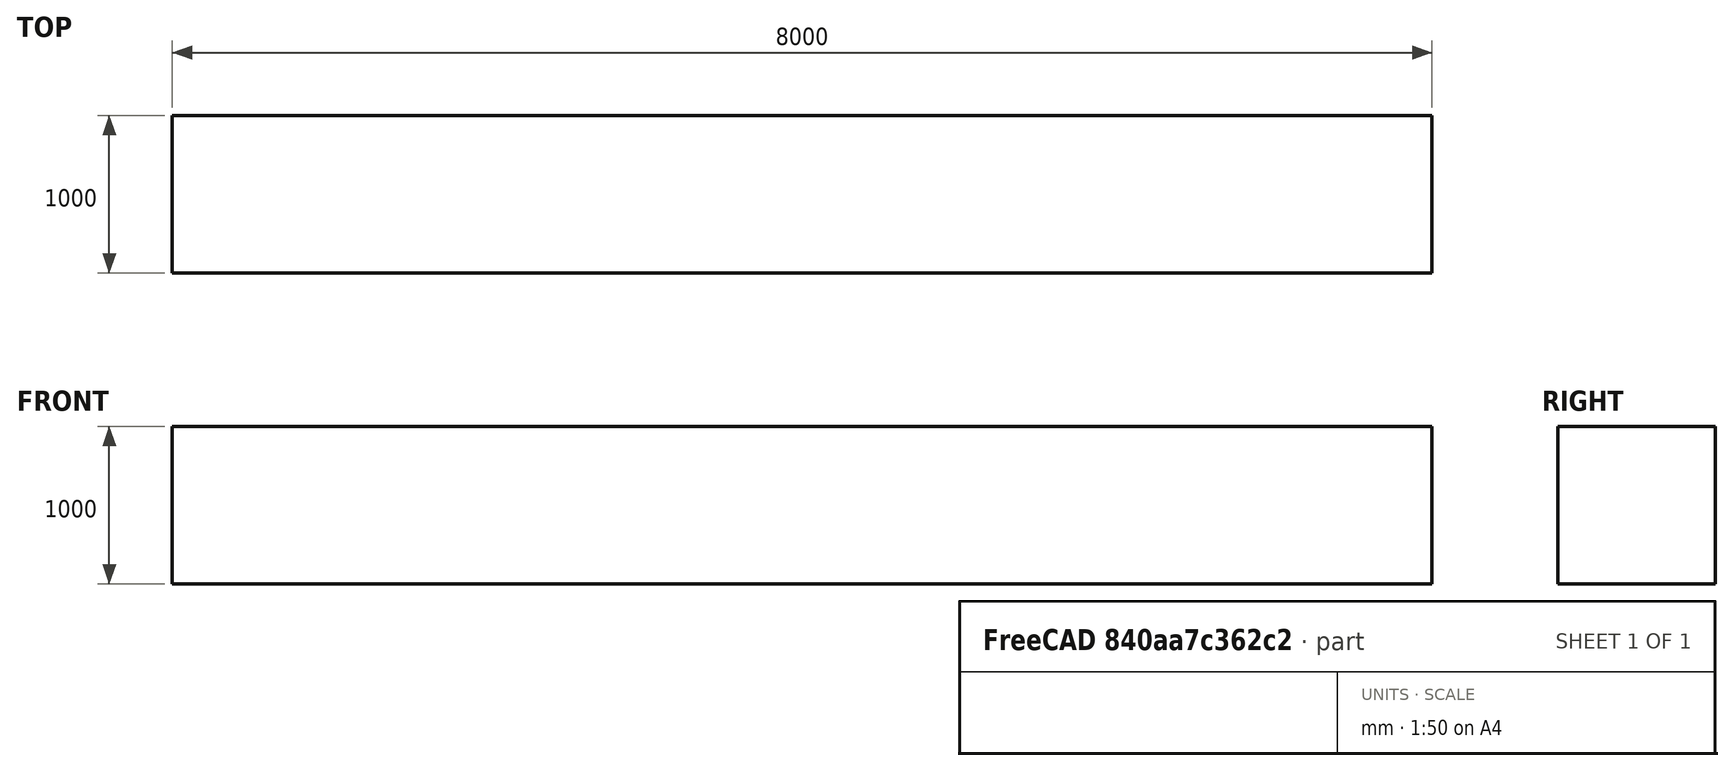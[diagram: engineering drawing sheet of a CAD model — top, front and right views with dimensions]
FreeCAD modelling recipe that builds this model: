
FCSTD DOCUMENT  (FreeCAD 0.19R17171 (Git))
Label: FemCalculixCantilever3D_newSolver
License: CC-BY 3.0
LicenseURL: http://creativecommons.org/licenses/by/3.0/
objects: Fem::FemSolverObjectPython×3, Fem::FemMeshObjectPython×3, Fem::FemResultObjectPython×2, Part::Box×1, Fem::ConstraintFixed×1, Fem::ConstraintForce×1, App::FeaturePython×1, App::MaterialObjectPython×1, Fem::FemPostPipeline×1, Fem::FemAnalysis×1
note: 1 computed .brp shape members not serialized (recipe doc carries the construction recipe); baked Part::Feature solids carry a one-line shape summary decoded from their .brp

FEATURE [Part::Box] Box  label="Cube"
  AttacherType = Attacher::AttachEngine3D
  Height = 1000
  Length = 8000
  Width = 1000
FEATURE [Fem::ConstraintFixed] FemConstraintFixed
  NormalDirection = (-1,0,0)
  Normals = (16) [(-1,0,0),(-1,0,0),(-1,0,0),(-1,0,0),(-1,0,0),(-1,0,0),(-1,0,0),(-1,0,0),(-1,0,0),(-1,0,0),(-1,0,0),(-1,0,0),(-1,0,0),(-1,0,0),(-1,0,0),(-1,0,0)]
  Points = (16) [(0,1000,0),(0,1000,333.333),(0,1000,666.667),(0,1000,1000),(0,666.667,0),(0,666.667,333.333),(0,666.667,666.667),(0,666.667,1000),(0,333.333,0),+7 more]
  References = -> [Box]
  Scale = 33
FEATURE [Fem::ConstraintForce] FemConstraintForce
  Direction = -> Box [Edge7]
  DirectionVector = (0,0,-1)
  Force = 9000000
  NormalDirection = (1,0,0)
  Points = (16) [(8000,1000,0),(8000,1000,333.333),(8000,1000,666.667),(8000,1000,1000),(8000,666.667,0),(8000,666.667,333.333),(8000,666.667,666.667),+9 more]
  References = -> [Box]
  Reversed = true
  Scale = 33
FEATURE [Fem::FemSolverObjectPython] SolverCalculiX  # FEM object (typed FeaturePython)
  AnalysisType = 0
  BeamShellResultOutput3D = false
  EigenmodeHighLimit = 0
  EigenmodeLowLimit = 0
  EigenmodesCount = 15
  GeometricalNonlinearity = 0
  IterationsControlParameterCutb = 0.25,0.5,0.75,0.85,,,1.5,
  IterationsControlParameterIter = 4,8,9,200,10,400,,200,,
  IterationsControlParameterTimeUse = false
  IterationsThermoMechMaximum = 2000
  IterationsUserDefinedIncrementations = false
  IterationsUserDefinedTimeStepLength = false
  MaterialNonlinearity = 0
  MatrixSolverType = 0
  SplitInputWriter = false
  ThermoMechSteadyState = true
  TimeEnd = 1
  TimeInitialStep = 1
FEATURE [Fem::FemSolverObjectPython] SolverZ88  # FEM object (typed FeaturePython)
  AnalysisType = 0
FEATURE [App::FeaturePython] Elasticity  # WARN: FeaturePython — macro-defined, semantics opaque (R4)
  BiCGstablDegree = 0
  Bubbles = false
  CalculatePangle = false
  CalculatePrincipal = false
  CalculateStrains = false
  CalculateStresses = false
  DoFrequencyAnalysis = false
  EigenmodesCount = 5
  LinearDirectMethod = 0
  LinearIterations = 500
  LinearIterativeMethod = 2
  LinearPreconditioning = 2
  LinearSolverType = 1
  LinearTolerance = 1e-08
  Priority = 10
  Stabilize = true
  SteadyStateTolerance = 1e-05
FEATURE [App::MaterialObjectPython] SolidMaterial  # material (typed FeaturePython)
  Category = 0
  Material = Density=7900.0 kg/m^3,Description=Standard steel material for CalculiX sample calculations,Father=Metal,Name=CalculiX-Steel,PoissonRatio=0.3,+4 more (map truncated)
FEATURE [Fem::FemMeshObjectPython] FEMMeshGmsh  # FEM object (typed FeaturePython)
  Algorithm2D = 0
  Algorithm3D = 0
  CharacteristicLengthMax = 0
  CharacteristicLengthMin = 0
  CoherenceMesh = true
  ElementDimension = 0
  ElementOrder = 1
  GeometryTolerance = 1e-06
  GroupsOfNodes = false
  HighOrderOptimize = false
  OptimizeNetgen = false
  OptimizeStd = true
  Part = -> Box
  RecombineAll = false
FEATURE [Fem::FemPostPipeline] SolverElmerResult
  Mode = 0
FEATURE [Fem::FemSolverObjectPython] SolverElmer  # FEM object (typed FeaturePython)
  ElmerResult = -> SolverElmerResult
  Group = -> [Elasticity]
  SteadyStateMaxIterations = 1
  SteadyStateMinIterations = 0
FEATURE [Fem::FemMeshObjectPython] Result_mesh  # FEM object (typed FeaturePython)
FEATURE [Fem::FemResultObjectPython] CalculiX_static_results  # FEM object (typed FeaturePython)
  DisplacementLengths = [0,0,0,0,87.937,87.9368,87.938,87.9383,0,0,0,0,0,0,0,0,0,0,0,0,87.5423,87.6436,87.6436,87.943,87.9418,87.9423,87.5435,87.6449,87.6448,87.9437,87.9421,87.9428,1.98318,5.68761,11.3939,18.906,28.0027,38.4037,49.8592,62.1074,74.8816,0.880806,+478 more]
  DisplacementVectors = (520) [(0,0,0),(0,0,0),(0,0,0),(0,0,0),(8.16317,0.00342817,-87.5573),(-8.1624,-0.00296136,-87.5572),(8.16362,-0.0026403,-87.5583),+513 more]
  Eigenmode = 0
  EigenmodeFrequency = 0
  MaxShear = [175.647,175.645,175.686,175.688,4.51499,4.58967,4.51746,4.67791,41.5712,86.6878,86.7027,145.847,146.892,146.912,41.5961,86.7112,86.7243,145.85,146.913,146.934,14.4288,9.69506,9.67773,6.30296,4.97789,5.00467,14.3519,9.6531,9.64731,6.38343,+490 more]
  Mesh = -> Result_mesh
  NodeNumbers = [1,2,3,4,5,6,7,8,9,10,11,12,13,14,15,16,17,18,19,20,21,22,23,24,25,26,27,28,29,30,31,32,33,34,35,36,37,38,39,40,41,42,43,44,45,46,47,48,49,50,51,52,53,54,55,56,57,58,59,60,61,62,63,64,65,66,67,68,69,+451 more]
  NodeStrainXX = [0.00178534,-0.00178542,0.0017858,-0.00178591,2.55731e-05,-2.6777e-05,2.60379e-05,-2.78694e-05,-6.62106e-08,-0.000893669,0.000893669,0.00158243,0.00162959,0.00162991,-4.29182e-08,-0.000893927,0.000893939,-0.00158248,-0.00162988,-0.00163023,+500 more]
  NodeStrainXY = [0.000338919,-0.000338841,-0.000338881,0.000338842,-6.24106e-06,7.20301e-06,5.95082e-06,-7.54054e-06,3.8554e-08,-0.000204328,0.000204485,1.06174e-07,0.000146602,-0.000146446,-4.03049e-08,0.000204291,-0.000204438,-8.30874e-08,-0.000146496,+501 more]
  NodeStrainXZ = [-6.75804e-05,-6.76787e-05,-6.76474e-05,-6.76703e-05,-1.60131e-05,-1.50392e-05,-1.61571e-05,-1.51969e-05,0.000257345,0.0002158,0.000215887,-0.000434903,-0.000376175,-0.000376179,0.0002575,0.000215933,0.000215976,-0.000434893,-0.000376205,+501 more]
  NodeStrainYY = [-0.000111636,0.000111593,-0.000111609,0.000111601,-3.55842e-06,3.91033e-06,-3.54351e-06,4.16606e-06,2.66083e-14,-6.95479e-10,6.95447e-10,1.51246e-09,1.57275e-09,1.57336e-09,-3.65614e-14,-6.95718e-10,6.95545e-10,-1.51159e-09,-1.57186e-09,+501 more]
  NodeStrainYZ = [-0.00011373,-0.000113706,0.00011372,0.000113715,-1.23872e-06,-4.54037e-07,4.7524e-07,-4.95007e-07,-1.76978e-10,-2.80391e-10,-2.80793e-10,-1.71255e-13,2.54542e-10,-2.54735e-10,1.76364e-10,2.79861e-10,2.80325e-10,-5.89765e-14,2.54579e-10,+501 more]
  NodeStrainZZ = [-0.000259206,0.000259149,-0.000259287,0.000259225,-1.85744e-05,1.95617e-05,-1.82326e-05,1.95673e-05,-4.52237e-13,-4.46011e-10,4.4508e-10,2.98021e-09,3.22873e-09,3.22896e-09,-2.82001e-13,-4.4624e-10,4.45783e-10,-2.98056e-09,-3.22912e-09,+501 more]
  NodeStressXX = [459.773,-459.807,459.898,-459.936,4.54783,-4.72592,4.72246,-5.00309,-0.0187173,-252.634,252.633,447.341,460.673,460.764,-0.0121327,-252.706,252.71,-447.355,-460.756,-460.854,-0.101075,-2.58096,2.3452,3.86865,4.10517,4.15412,0.000454672,+493 more]
  NodeStressXY = [54.7484,-54.7359,-54.7423,54.7361,-1.00817,1.16356,0.961287,-1.21809,0.00622796,-33.0068,33.0321,0.0171512,23.6819,-23.6567,-0.00651079,33.0008,-33.0246,-0.0134218,-23.6648,23.6443,-0.131759,0.240361,-0.375904,0.00314049,-0.486655,0.488129,+494 more]
  NodeStressXZ = [-10.9168,-10.9327,-10.9277,-10.9313,-2.58673,-2.42941,-2.61,-2.45489,41.5712,34.86,34.8741,-70.2536,-60.7668,-60.7673,41.5961,34.8815,34.8884,-70.2519,-60.7716,-60.7698,-14.3132,-8.75048,-8.75272,-3.91196,-2.86704,-2.85839,-14.2385,+493 more]
  NodeStressYY = [153.338,-153.367,153.392,-153.415,-0.158025,0.231264,-0.0560809,0.171878,-0.00802172,-108.272,108.272,191.718,197.432,197.471,-0.00519975,-108.303,108.304,-191.724,-197.467,-197.509,-0.122017,0.26783,-0.398508,-2.65084,-1.20161,-1.23923,+494 more]
  NodeStressYZ = [-18.3718,-18.3679,18.3702,18.3693,-0.200101,-0.0733444,0.0767696,-0.0799626,-2.85888e-05,-4.52939e-05,-4.53589e-05,-2.76643e-08,4.11184e-05,-4.11495e-05,2.84895e-05,4.52083e-05,4.52832e-05,-9.52698e-09,4.11244e-05,-4.11204e-05,-1.81789,+499 more]
  NodeStressZZ = [129.5,-129.531,129.537,-129.568,-2.58368,2.75957,-2.42894,2.65977,-0.0080218,-108.272,108.272,191.718,197.432,197.471,-0.00519978,-108.303,108.304,-191.724,-197.468,-197.51,-0.145698,5.56072,-5.70667,-6.01543,-3.93908,-3.96064,0.0607276,+493 more]
  PrincipalMax = [469.829,-118.571,469.951,-118.61,5.5295,3.52963,5.71143,3.40171,41.5578,-93.7652,267.155,465.377,475.945,476.029,41.5874,-93.7933,267.231,-173.69,-182.199,-182.248,14.2888,11.2181,7.95689,5.22956,5.07933,5.11797,14.3761,11.1891,8.09282,+491 more]
  PrincipalMed = [154.247,-154.274,154.297,-154.323,-0.222903,0.384978,-0.1505,0.380942,-0.00802171,-108.272,108.272,191.718,197.432,197.471,-0.00519974,-108.303,108.304,-191.724,-197.467,-197.509,-0.0887516,0.201412,-0.318296,-2.65082,-1.2384,-1.27234,+494 more]
  PrincipalMin = [118.534,-469.86,118.58,-469.986,-3.50047,-5.6497,-3.32349,-5.9541,-41.5846,-267.141,93.7498,173.682,182.16,182.206,-41.6048,-267.216,93.7827,-465.389,-476.025,-476.116,-14.5688,-8.17197,-11.3986,-7.37636,-4.87645,-4.89138,-14.3278,-8.11712,+492 more]
  ResultType = Fem::FemResultMechanical
  Stats = [-8.16894,-6.16628e-06,8.16895,-0.266968,-2.61048e-05,0.266841,-87.5635,-34.8376,0,0,35.1365,87.9437,2.27927,136.634,438.103,-182.248,69.4964,476.029,-197.509,0.0271809,197.471,-476.116,-69.5959,182.206,1.31593,69.5461,226.848,0,0,0,0,0,0,0,+5 more]
  StressValues = [334.87,334.868,334.944,334.951,7.91748,8.0798,7.93914,8.2701,72.0034,166.596,166.62,283.107,286.454,286.496,72.0466,166.642,166.663,283.113,286.497,286.542,24.9914,16.8443,16.8209,11.0304,8.72544,8.7784,24.8584,16.7689,16.7557,11.1209,+490 more]
  Time = 0
FEATURE [Fem::FemMeshObjectPython] Result_mesh001  # FEM object (typed FeaturePython)
FEATURE [Fem::FemResultObjectPython] Z88_static_results  # FEM object (typed FeaturePython)
  DisplacementVectors = (520) [(0,0,0),(0,0,0),(0,0,0),(0,0,0),(8.16317,0.00342817,-87.5573),(-8.1624,-0.00296136,-87.5572),(8.16362,-0.0026403,-87.5583),+513 more]
  Eigenmode = 0
  EigenmodeFrequency = 0
  Mesh = -> Result_mesh001
  NodeNumbers = [1,2,3,4,5,6,7,8,9,10,11,12,13,14,15,16,17,18,19,20,21,22,23,24,25,26,27,28,29,30,31,32,33,34,35,36,37,38,39,40,41,42,43,44,45,46,47,48,49,50,51,52,53,54,55,56,57,58,59,60,61,62,63,64,65,66,67,68,69,+451 more]
  ResultType = Fem::FemResultMechanical
  Stats = [0,0,0,0,0,0,0,0,0,0,0,0,0,0,0,0,0,0,0,0,0,0,0,0,0,0,0,0,0,0,0,0,0,0,0,0,0,0,0]
  Time = 0
FEATURE [Fem::FemAnalysis] Analysis
  Group = -> [SolverCalculiX,SolverZ88,SolverElmer,SolidMaterial,FemConstraintFixed,FemConstraintForce,FEMMeshGmsh,SolverElmerResult,CalculiX_static_results,Z88_static_results]
